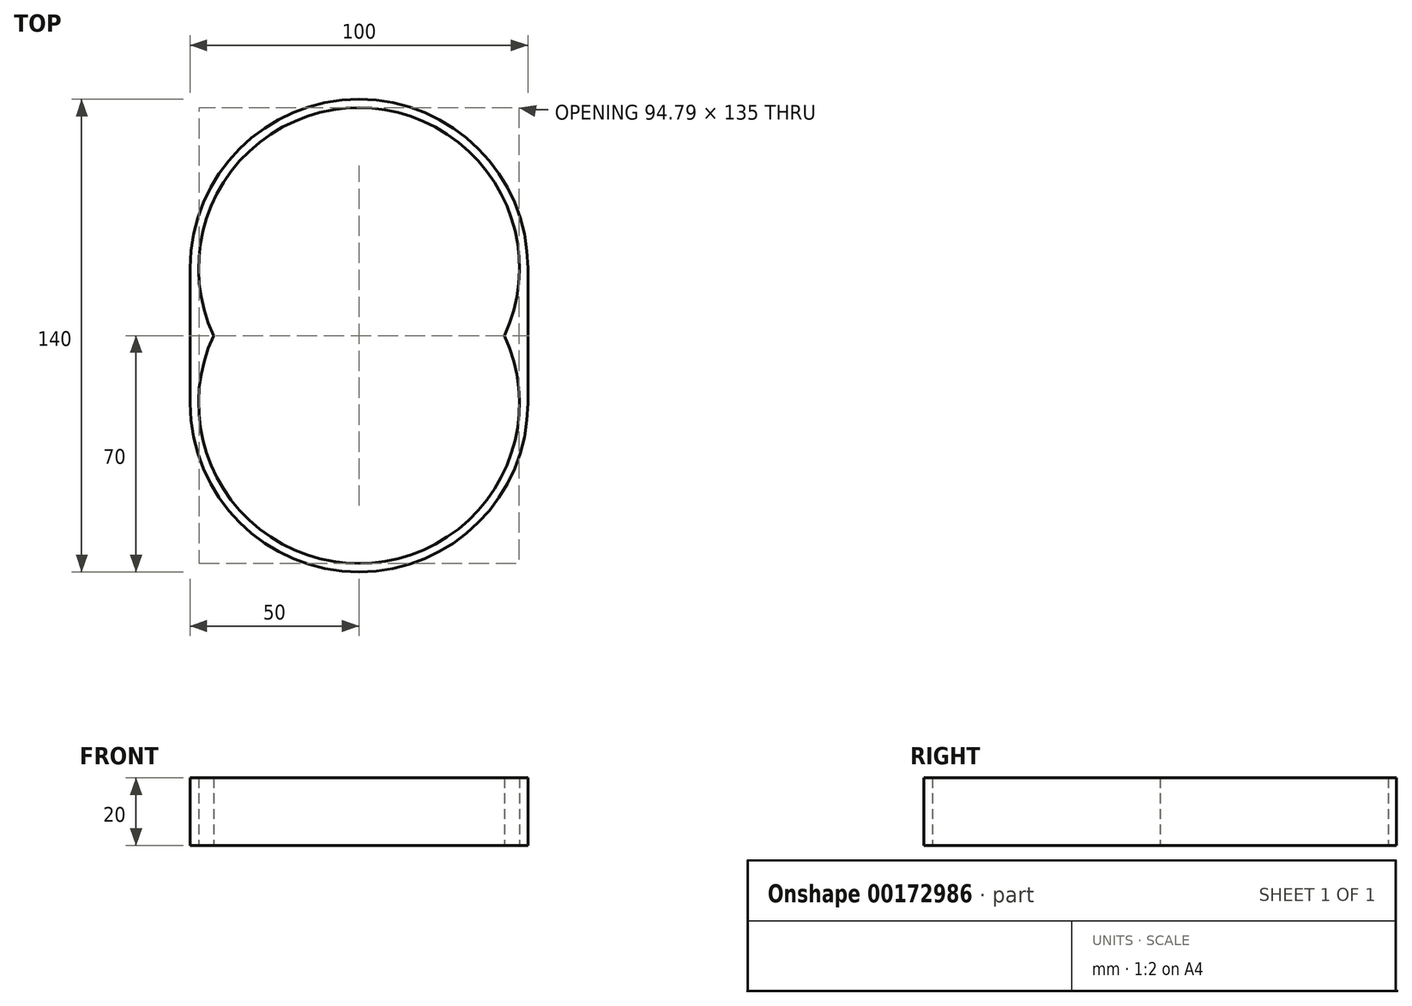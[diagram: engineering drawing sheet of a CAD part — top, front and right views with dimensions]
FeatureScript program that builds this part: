
annotation { "Feature Type Name" : "Feature", "Feature Type Description" : "" }
export const myFeature = defineFeature(function(context is Context, id is Id, definition is map)
    precondition{}
    {
        {
            var Q0;
            Q0=qCreatedBy(makeId("Top.planeOp"),FACE);
            var sketch = newSketch(context, id + "F0", { "sketchPlane" : qUnion([Q0])});
            skCircle(sketch, "E0", {"center": v(0, 0) * mm, "radius": 47.5 * mm});
            skCircle(sketch, "E1", {"center": v(0, -40) * mm, "radius": 47.5 * mm});
            skSolve(sketch);
        }
        {
            var Q0;
            Q0=qCreatedBy(makeId("Top.planeOp"),FACE);
            var sketch = newSketch(context, id + "F1", { "sketchPlane" : qUnion([Q0])});
            skCircle(sketch, "E2", {"center": v(0, 0) * mm, "radius": 50 * mm});
            skCircle(sketch, "E3", {"center": v(0, -40) * mm, "radius": 50 * mm});
            skLineSegment(sketch, "E4", {"start": v(-50, 0) * mm, "end": v(-50, -40) * mm});
            skLineSegment(sketch, "E5", {"start": v(0, 41.82) * mm, "end": v(0, -72) * mm, "construction": true});
            skLineSegment(sketch, "E6.MirrorCS", {"start": v(50, 0) * mm, "end": v(50, -40) * mm});
            skSolve(sketch);
        }
        {
            var Q0;
            {var subQ0=sQuery(id+"F1.wireOp",EDGE,"E3");var subQ1=sQuery(id+"F1.wireOp",EDGE,"E2");var subQ2=makeQuery(id+"F1.imprint","INTERSECT",VERTEX,{"disambiguationData":[OD(0.0)],"derivedFrom":[subQ1,subQ0]});Q0=makeQuery(id+"F1.imprint","IMPRINT",FACE,{"disambiguationData":[TD([[makeQuery(id+"F1.imprint","IMPRINT",EDGE,{"disambiguationData":[TD([[subQ2,-1.0]])],"derivedFrom":subQ1}),1.0]])]});}
            extrude(context, id + "F2", {"entities" : qUnion([Q0]), "depth" : 20 * mm});
        }
        {
            var Q0;
            Q0 = qSketchRegion(id + "F1", true);
            extrude(context, id + "F3", {"entities" : qUnion([Q0]), "operationType" : NewBodyOperationType.ADD, "depth" : 20 * mm});
        }
        {
            var Q0;
            Q0 = qSketchRegion(id + "F0", true);
            extrude(context, id + "F4", {"entities" : qUnion([Q0]), "operationType" : NewBodyOperationType.REMOVE, "depth" : 20 * mm});
        }
    });
